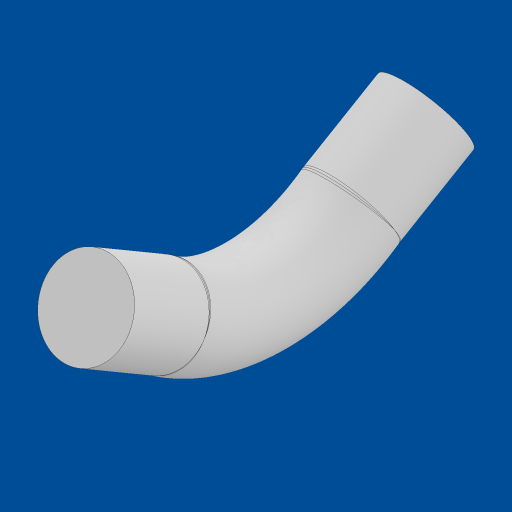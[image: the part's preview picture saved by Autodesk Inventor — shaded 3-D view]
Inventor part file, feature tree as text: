
AUTODESK INVENTOR PART (.ipt)
format: ipt  version: 2023 (Build 270158000, 158)  size: 158,208 bytes
history: native  units: mm
features: sketch x5, plane x2, extrude x2, sweep x1
ambient origin geometry x8: Origin, YZ Plane, XZ Plane, XY Plane, X Axis, Y Axis, Z Axis, Center Point
bodies: Solid1 (feature_tree)
feature tree (10):
  sketch  "Sketch1"  dims[d4=5.5mm d5=50.0mm d6=11.0mm]
  plane  "Work Plane2"
  sketch  "Sketch2"  dims[d7=11.0mm d8=0.0mm d9=11.0mm]
  extrude  "Extrusion1"  Depth=11.0mm
  plane  "Work Plane3"
  extrude  "Extrusion2"  Depth=11.0mm
  sweep  "Sweep1"
  sketch  "Sketch5"  dims[d17=5.5mm]
  sketch  "Sketch6"  dims[d18=5.5mm d19=11.0mm d20=11.0mm]
  sketch  "Sketch3"  dims[d10=11.0mm d11=0.0mm d12=0.0mm d13=0.0mm]
